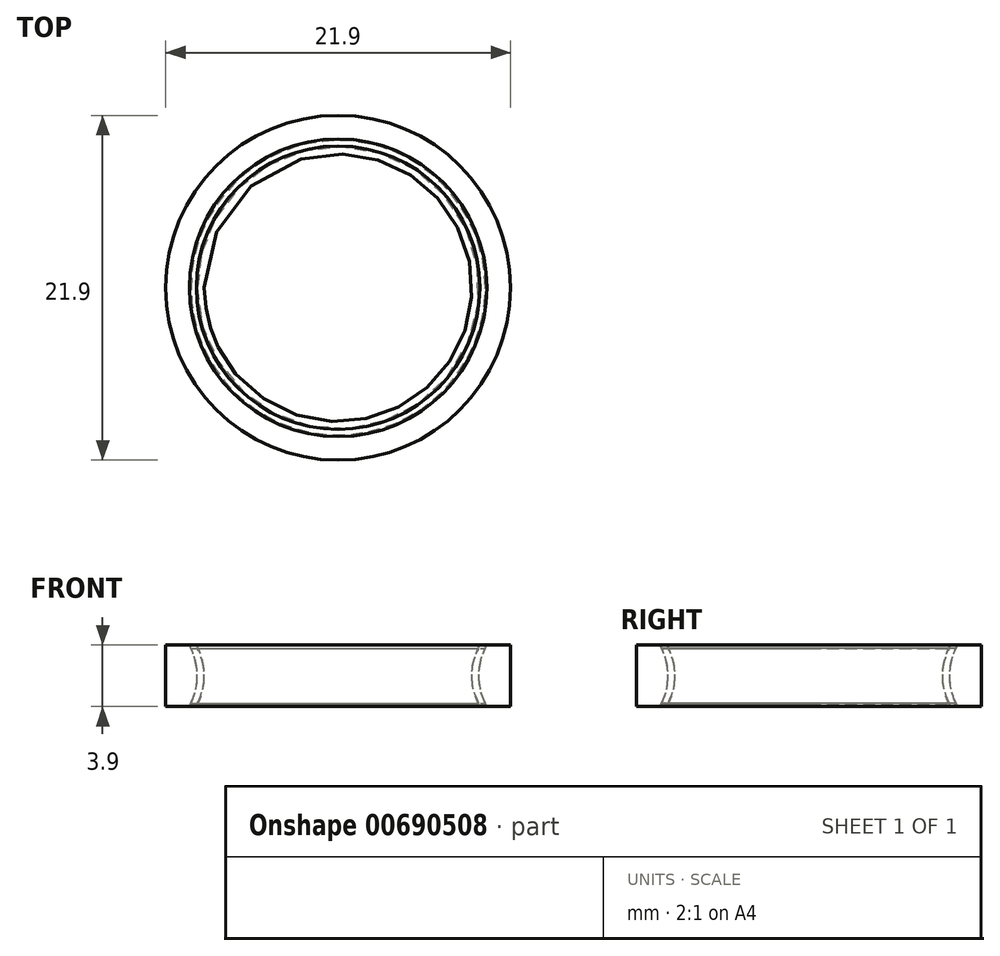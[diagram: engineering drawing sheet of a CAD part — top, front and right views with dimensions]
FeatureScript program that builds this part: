
annotation { "Feature Type Name" : "Feature", "Feature Type Description" : "" }
export const myFeature = defineFeature(function(context is Context, id is Id, definition is map)
    precondition{}
    {
        {
            var Q0;
            Q0=qCreatedBy(makeId("Front.planeOp"),FACE);
            var sketch = newSketch(context, id + "F0", { "sketchPlane" : qUnion([Q0])});
            skLineSegment(sketch, "E0", {"start": v(0, 0) * mm, "end": v(8.95, 0) * mm, "construction": true});
            skLineSegment(sketch, "E1", {"start": v(9.45, 1.95) * mm, "end": v(10.95, 1.95) * mm});
            skLineSegment(sketch, "E2", {"start": v(10.95, 1.95) * mm, "end": v(10.95, -1.95) * mm});
            skLineSegment(sketch, "E3", {"start": v(10.95, -1.95) * mm, "end": v(9.45, -1.95) * mm});
            skArc(sketch, "E4", {"start": v(9.45, 1.95) * mm, "mid": v(8.95, 0) * mm, "end": v(9.45, -1.95) * mm});
            skLineSegment(sketch, "E5", {"start": v(0, 0) * mm, "end": v(0, 1.95) * mm, "construction": true});
            skLineSegment(sketch, "E6", {"start": v(8.95, 0) * mm, "end": v(8.95, 1.95) * mm, "construction": true});
            skLineSegment(sketch, "E7", {"start": v(8.95, 1.95) * mm, "end": v(9.45, 1.95) * mm, "construction": true});
            skSolve(sketch);
        }
        {
            var Q0;
            Q0=makeQuery(id+"F0.imprint","IMPRINT",FACE,{"disambiguationData":[TD([[makeQuery(id+"F0.imprint","IMPRINT",EDGE,{"derivedFrom":sQuery(id+"F0.wireOp",EDGE,"E1")}),-1.0]])]});
            var Q1;
            Q1=sQuery(id+"F0.wireOp",EDGE,"E5");
            revolve(context, id + "F1", {"entities" : qUnion([Q0]), "axis" : qUnion([Q1]), "revolveType" : RevolveType.FULL});
        }
        {
            var Q0;
            Q0=qCreatedBy(makeId("Front.planeOp"),FACE);
            var sketch = newSketch(context, id + "F2", { "sketchPlane" : qUnion([Q0])});
            skLineSegment(sketch, "E8", {"start": v(0, 0) * mm, "end": v(0, 1.48) * mm, "construction": true});
            skLineSegment(sketch, "E9", {"start": v(0, 0) * mm, "end": v(8.5, 0) * mm, "construction": true});
            skLineSegment(sketch, "E10", {"start": v(9, 1.95) * mm, "end": v(10.5, 1.95) * mm});
            skLineSegment(sketch, "E11", {"start": v(10.5, 1.95) * mm, "end": v(10.5, -1.95) * mm});
            skLineSegment(sketch, "E12", {"start": v(10.5, -1.95) * mm, "end": v(9, -1.95) * mm});
            skArc(sketch, "E13", {"start": v(9, 1.95) * mm, "mid": v(8.5, 0) * mm, "end": v(9, -1.95) * mm});
            skLineSegment(sketch, "E14", {"start": v(8.5, 0) * mm, "end": v(8.5, 1.95) * mm, "construction": true});
            skLineSegment(sketch, "E15", {"start": v(8.5, 1.95) * mm, "end": v(9, 1.95) * mm, "construction": true});
            skSolve(sketch);
        }
        {
            var Q0;
            Q0=makeQuery(id+"F0.imprint","IMPRINT",FACE,{"disambiguationData":[TD([[makeQuery(id+"F0.imprint","IMPRINT",EDGE,{"derivedFrom":sQuery(id+"F0.wireOp",EDGE,"E1")}),-1.0]])]});
            var sketch = newSketch(context, id + "F3", { "sketchPlane" : qUnion([Q0])});
            skLineSegment(sketch, "E16", {"start": v(9.35, -1.75) * mm, "end": v(8.95, -1.75) * mm});
            skArc(sketch, "E17", {"start": v(9.45, 1.95) * mm, "mid": v(8.95, 0) * mm, "end": v(9.45, -1.95) * mm});
            skLineSegment(sketch, "E18", {"start": v(9.35, 1.75) * mm, "end": v(8.95, 1.75) * mm});
            skArc(sketch, "E19", {"start": v(8.5, 0) * mm, "mid": v(8.61, -0.9) * mm, "end": v(8.95, -1.75) * mm});
            skArc(sketch, "E20", {"start": v(8.95, 1.75) * mm, "mid": v(8.61, 0.9) * mm, "end": v(8.5, 0) * mm});
            skLineSegment(sketch, "E21", {"start": v(8.95, 1.75) * mm, "end": v(8.95, 1.95) * mm, "construction": true});
            skLineSegment(sketch, "E22", {"start": v(8.95, -1.75) * mm, "end": v(8.95, -1.95) * mm, "construction": true});
            skSolve(sketch);
        }
        {
            var Q0;
            {var subQ2=sQuery(id+"F3.wireOp",EDGE,"E16");Q0=makeQuery(id+"F3.imprint","IMPRINT",FACE,{"disambiguationData":[TD([[makeQuery(id+"F3.imprint","IMPRINT",EDGE,{"derivedFrom":subQ2}),-1.0]])]});}
            var Q1;
            Q1=sQuery(id+"F0.wireOp",EDGE,"E5");
            revolve(context, id + "F4", {"surfaceOperationType" : NewSurfaceOperationType.NEW, "entities" : qUnion([Q0]), "axis" : qUnion([Q1]), "revolveType" : RevolveType.FULL});
        }
        {
            var Q0;
            Q0=makeQuery(id+"F2.imprint","IMPRINT",FACE,{"disambiguationData":[TD([[makeQuery(id+"F2.imprint","IMPRINT",EDGE,{"derivedFrom":sQuery(id+"F2.wireOp",EDGE,"E10")}),-1.0]])]});
            var Q1;
            Q1=sQuery(id+"F2.wireOp",EDGE,"E8");
            revolve(context, id + "F5", {"entities" : qUnion([Q0]), "axis" : qUnion([Q1]), "revolveType" : RevolveType.FULL});
        }
        {
            var Q0;
            Q0=makeQuery(id+"F1.opRevolve","SWEPT_BODY",BODY,{"disambiguationData":[OSD([sQuery(id+"F0.wireOp",EDGE,"E1"),sQuery(id+"F0.wireOp",EDGE,"E2"),sQuery(id+"F0.wireOp",EDGE,"E3"),sQuery(id+"F0.wireOp",EDGE,"E4")])]});
            var Q1;
            Q1=makeQuery(id+"F5.opRevolve","SWEPT_BODY",BODY,{"disambiguationData":[OSD([sQuery(id+"F2.wireOp",EDGE,"E10"),sQuery(id+"F2.wireOp",EDGE,"E11"),sQuery(id+"F2.wireOp",EDGE,"E12"),sQuery(id+"F2.wireOp",EDGE,"E13")])]});
            booleanBodies(context, id + "F6", {"operationType" : BooleanOperationType.SUBTRACTION, "tools" : qUnion([Q0]), "targets" : qUnion([Q1]), "keepTools" : true});
        }
    });
